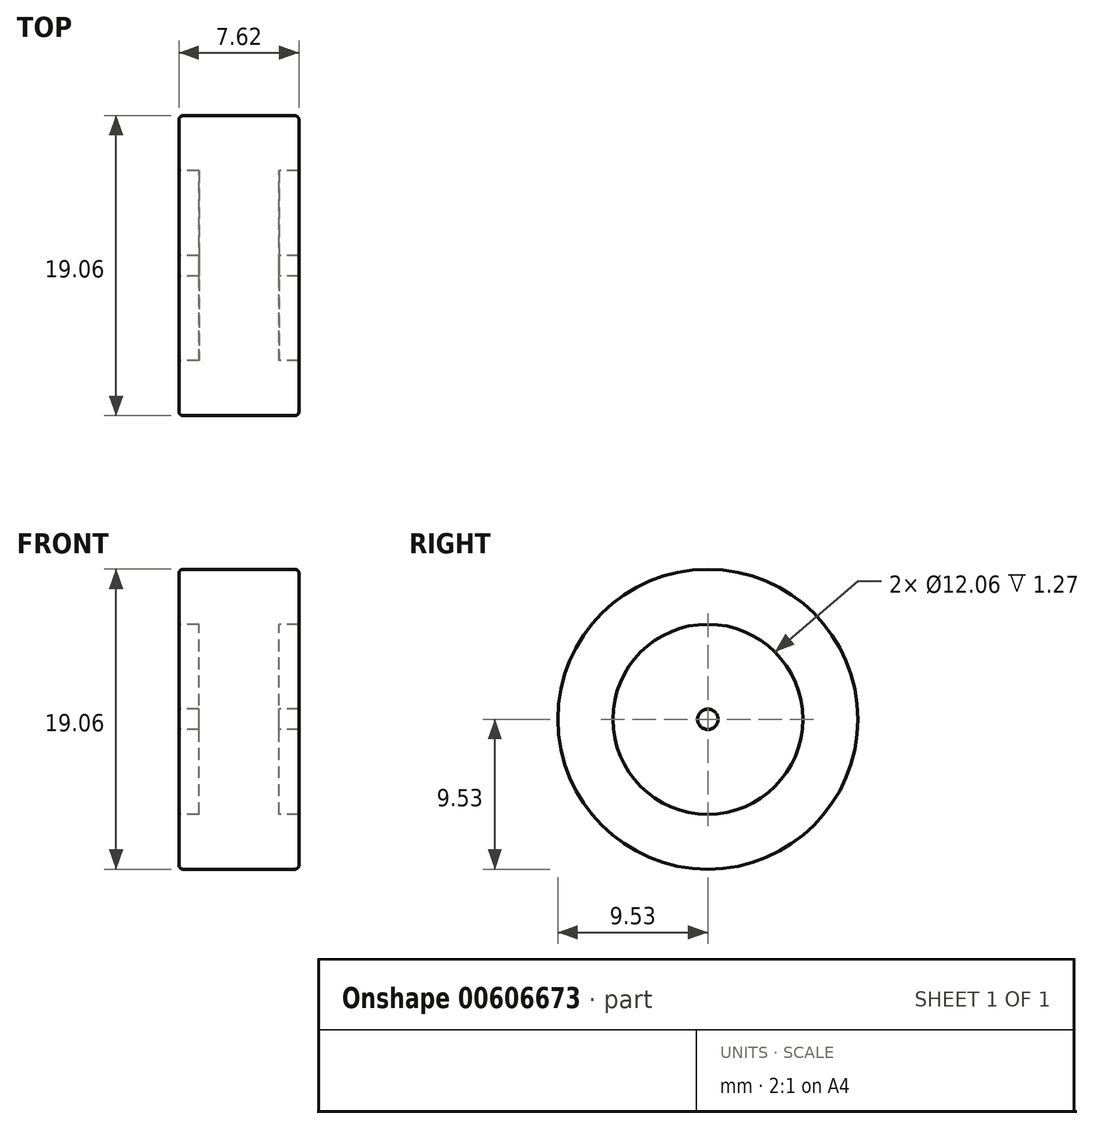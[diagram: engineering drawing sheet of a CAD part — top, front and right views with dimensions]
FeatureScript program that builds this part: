
annotation { "Feature Type Name" : "Feature", "Feature Type Description" : "" }
export const myFeature = defineFeature(function(context is Context, id is Id, definition is map)
    precondition{}
    {
        {
            var Q0;
            Q0=qCreatedBy(makeId("Right.planeOp"),FACE);
            var sketch = newSketch(context, id + "F0", { "sketchPlane" : qUnion([Q0])});
            skCircle(sketch, "E0", {"center": v(0, 0) * mm, "radius": 9.53 * mm});
            skCircle(sketch, "E1", {"center": v(0, 0) * mm, "radius": 6.03 * mm});
            skCircle(sketch, "E2", {"center": v(0, 0) * mm, "radius": 0.65 * mm});
            skSolve(sketch);
        }
        {
            var Q0;
            Q0=makeQuery(id+"F0.imprint","IMPRINT",FACE,{"disambiguationData":[TD([[makeQuery(id+"F0.imprint","IMPRINT",EDGE,{"derivedFrom":sQuery(id+"F0.wireOp",EDGE,"E2")}),1.0]])]});
            extrude(context, id + "F1", {"entities" : qUnion([Q0]), "endBound" : BoundingType.SYMMETRIC, "depth" : 7.62 * mm, "offsetDistance" : 25.4 * mm});
        }
        {
            var Q0;
            Q0=makeQuery(id+"F0.imprint","IMPRINT",FACE,{"disambiguationData":[TD([[makeQuery(id+"F0.imprint","IMPRINT",EDGE,{"derivedFrom":sQuery(id+"F0.wireOp",EDGE,"E1")}),1.0]])]});
            extrude(context, id + "F2", {"entities" : qUnion([Q0]), "operationType" : NewBodyOperationType.ADD, "endBound" : BoundingType.SYMMETRIC, "depth" : 5.08 * mm, "offsetDistance" : 25.4 * mm});
        }
        {
            var Q0;
            Q0=makeQuery(id+"F0.imprint","IMPRINT",FACE,{"disambiguationData":[TD([[makeQuery(id+"F0.imprint","IMPRINT",EDGE,{"derivedFrom":sQuery(id+"F0.wireOp",EDGE,"E0")}),1.0]])]});
            extrude(context, id + "F3", {"entities" : qUnion([Q0]), "operationType" : NewBodyOperationType.ADD, "endBound" : BoundingType.SYMMETRIC, "depth" : 7.62 * mm, "offsetDistance" : 25.4 * mm});
        }
        {
            var Q0;
            Q0=makeQuery(id+"F3.opExtrude","CAP_EDGE",EDGE,{"disambiguationData":[OSD([sQuery(id+"F0.wireOp",EDGE,"E0")])],"isStart":false});
            var Q1;
            Q1=makeQuery(id+"F3.opExtrude","CAP_EDGE",EDGE,{"disambiguationData":[OSD([sQuery(id+"F0.wireOp",EDGE,"E0")])],"isStart":true});
            fillet(context, id + "F4", {"entities" : qUnion([Q0, Q1]), "tangentPropagation" : true, "radius" : 0.25 * mm, "defaultsChanged" : true, "vertexSettings" : [], "allowEdgeOverflow" : false});
        }
    });
